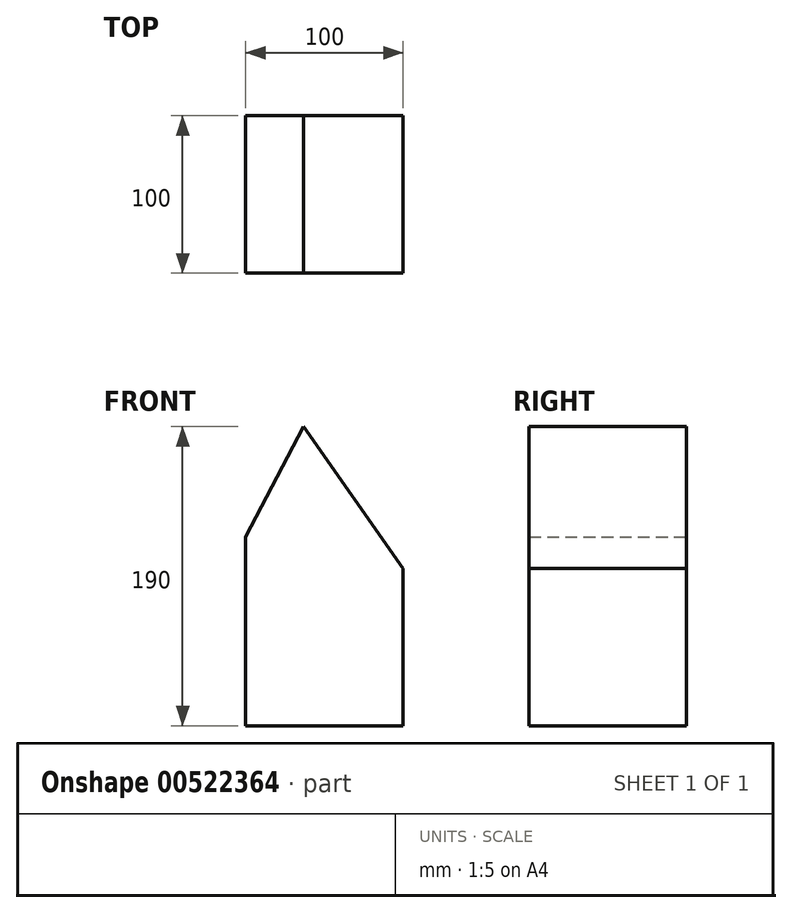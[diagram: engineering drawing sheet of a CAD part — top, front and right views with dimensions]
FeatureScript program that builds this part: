
annotation { "Feature Type Name" : "Feature", "Feature Type Description" : "" }
export const myFeature = defineFeature(function(context is Context, id is Id, definition is map)
    precondition{}
    {
        {
            var Q0;
            Q0=qCreatedBy(makeId("Front.planeOp"),FACE);
            var sketch = newSketch(context, id + "F0", { "sketchPlane" : qUnion([Q0])});
            skLineSegment(sketch, "E0", {"start": v(-50, -39.65) * mm, "end": v(50, -39.65) * mm});
            skLineSegment(sketch, "E1", {"start": v(-50, -39.65) * mm, "end": v(-50, 80.35) * mm});
            skLineSegment(sketch, "E2", {"start": v(50, -39.65) * mm, "end": v(50, 60.35) * mm});
            skLineSegment(sketch, "E3", {"start": v(-50, 80.35) * mm, "end": v(-13.27, 150.35) * mm});
            skLineSegment(sketch, "E4", {"start": v(-13.27, 150.35) * mm, "end": v(50, 60.35) * mm});
            skSolve(sketch);
        }
        {
            var Q0;
            Q0=makeQuery(id+"F0.imprint","IMPRINT",FACE,{"disambiguationData":[TD([[makeQuery(id+"F0.imprint","IMPRINT",EDGE,{"derivedFrom":sQuery(id+"F0.wireOp",EDGE,"E0")}),1.0]])]});
            extrude(context, id + "F1", {"entities" : qUnion([Q0]), "depth" : 100 * mm, "offsetDistance" : 25 * mm});
        }
    });
